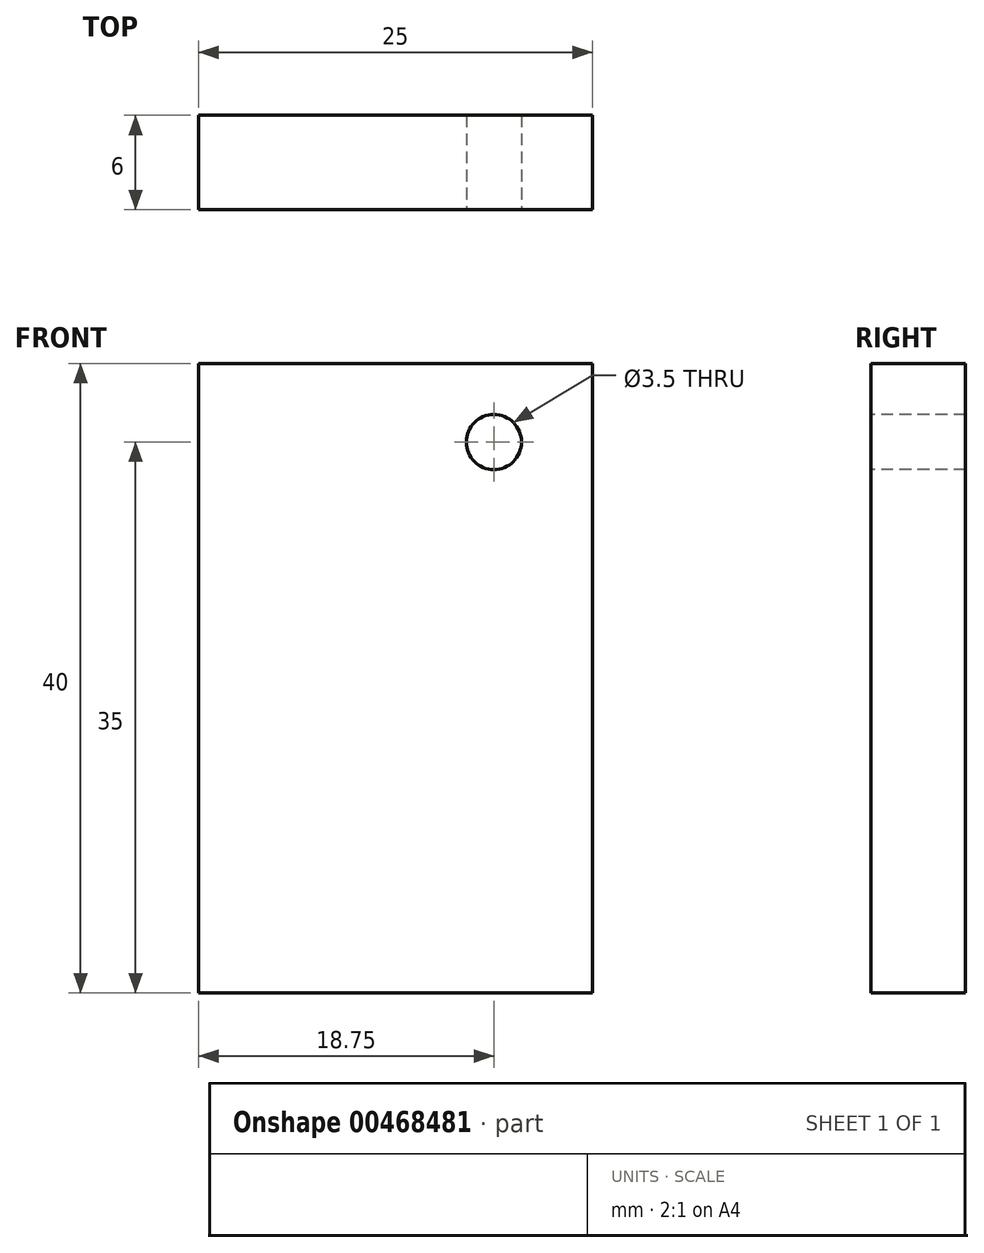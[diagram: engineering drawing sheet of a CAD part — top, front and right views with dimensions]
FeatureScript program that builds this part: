
annotation { "Feature Type Name" : "Feature", "Feature Type Description" : "" }
export const myFeature = defineFeature(function(context is Context, id is Id, definition is map)
    precondition{}
    {
        {
            var Q0;
            Q0=qCreatedBy(makeId("Front.planeOp"),FACE);
            var sketch = newSketch(context, id + "F0", { "sketchPlane" : qUnion([Q0])});
            skLineSegment(sketch, "E0.bottom", {"start": v(-12.5, 10) * mm, "end": v(12.5, 10) * mm});
            skLineSegment(sketch, "E0.top", {"start": v(-12.5, -30) * mm, "end": v(12.5, -30) * mm});
            skLineSegment(sketch, "E0.left", {"start": v(-12.5, 10) * mm, "end": v(-12.5, -30) * mm});
            skLineSegment(sketch, "E0.right", {"start": v(12.5, 10) * mm, "end": v(12.5, -30) * mm});
            skLineSegment(sketch, "E1", {"start": v(0, 31.9) * mm, "end": v(0, -31.9) * mm, "construction": true});
            skLineSegment(sketch, "E2", {"start": v(-31.9, 0) * mm, "end": v(31.9, 0) * mm, "construction": true});
            skCircle(sketch, "E3", {"center": v(-6.25, 5) * mm, "radius": 1.75 * mm});
            skCircle(sketch, "E4.MirrorC", {"center": v(6.25, 5) * mm, "radius": 1.75 * mm});
            skSolve(sketch);
        }
        {
            var Q0;
            Q0 = qSketchRegion(id + "F0", true);
            var Q1;
            Q1=makeQuery(id+"F0.imprint","IMPRINT",FACE,{"disambiguationData":[TD([[makeQuery(id+"F0.imprint","IMPRINT",EDGE,{"derivedFrom":sQuery(id+"F0.wireOp",EDGE,"E3")}),1.0]])]});
            var Q2;
            Q2=makeQuery(id+"F0.imprint","IMPRINT",FACE,{"disambiguationData":[TD([[makeQuery(id+"F0.imprint","IMPRINT",EDGE,{"derivedFrom":sQuery(id+"F0.wireOp",EDGE,"E4.MirrorC")}),-1.0]])]});
            extrude(context, id + "F1", {"entities" : qUnion([Q0, Q1, Q2]), "oppositeDirection" : true, "depth" : 3 * mm});
        }
        {
            var Q0;
            Q0=makeQuery(id+"F0.imprint","IMPRINT",FACE,{"disambiguationData":[TD([[makeQuery(id+"F0.imprint","IMPRINT",EDGE,{"derivedFrom":sQuery(id+"F0.wireOp",EDGE,"E3")}),1.0]])]});
            var Q1;
            Q1=makeQuery(id+"F0.imprint","IMPRINT",FACE,{"disambiguationData":[TD([[makeQuery(id+"F0.imprint","IMPRINT",EDGE,{"derivedFrom":sQuery(id+"F0.wireOp",EDGE,"E4.MirrorC")}),-1.0]])]});
            extrude(context, id + "F2", {"entities" : qUnion([Q0, Q1]), "operationType" : NewBodyOperationType.ADD, "depth" : 3 * mm});
        }
    });
